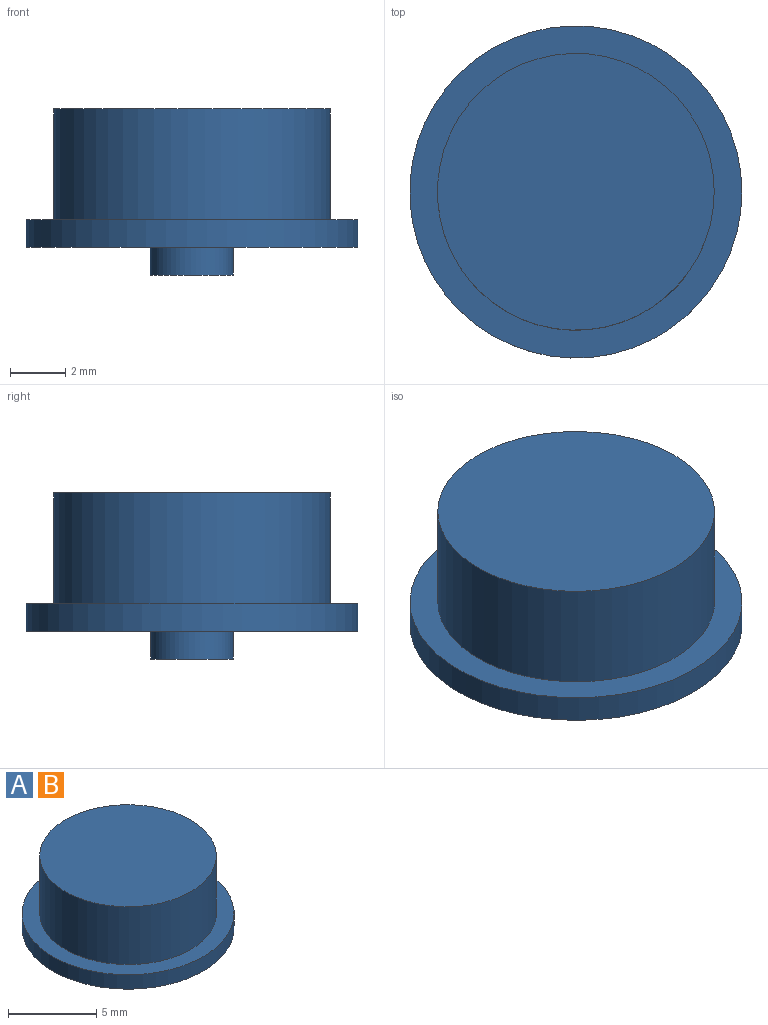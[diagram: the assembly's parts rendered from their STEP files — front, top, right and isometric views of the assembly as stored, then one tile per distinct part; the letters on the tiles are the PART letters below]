
ASSEMBLY  parts=2 mates=1
PART A: 7 faces, bbox 12x12x6 mm
  f0: plane 3x3mm, normal (0,0,-1), area 7.1mm2, adj f6
  f1: plane 10x10mm, normal (0,0,1), area 78.5mm2, adj f2
  f2: cylinder r=5mm len=10mm, axis (0,0,1), area 125.7mm2, adj f1,f3
  f3: plane 12x12mm, normal (0,0,1), area 34.6mm2, adj f2,f4
  f4: cylinder r=6mm len=12mm, axis (0,0,1), area 37.7mm2, adj f3,f5
  f5: plane 12x12mm, normal (0,0,-1), area 106mm2, adj f4,f6
  f6: cylinder r=1.5mm len=3mm, axis (0,0,1), area 9.4mm2, adj f0,f5
PART B: same geometry as A
PLACE A t=(-0.79,1.65,0.16)mm
PLACE B t=(-0.79,1.65,0.16)mm
MATE slider A.f2 <-> B.f2  axis (0,0,1) through (-0.79,1.65,6.16)mm
